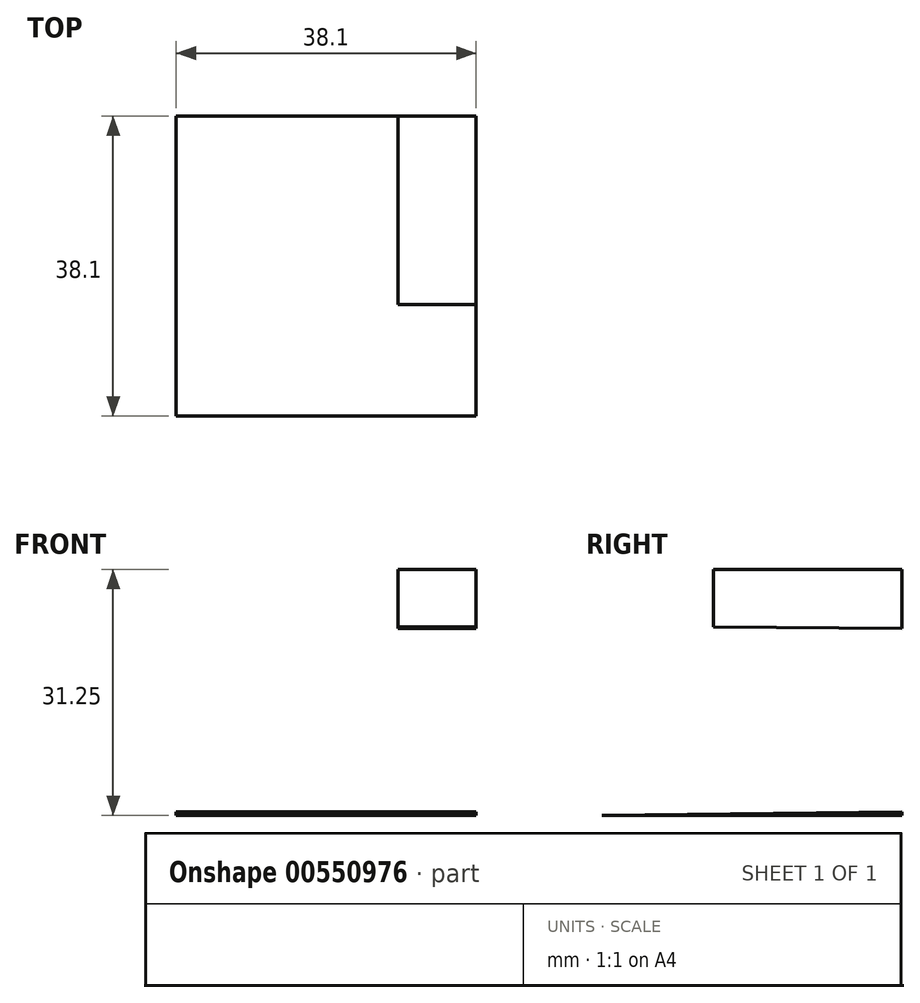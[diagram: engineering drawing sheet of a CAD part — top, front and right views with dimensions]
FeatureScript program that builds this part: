
annotation { "Feature Type Name" : "Feature", "Feature Type Description" : "" }
export const myFeature = defineFeature(function(context is Context, id is Id, definition is map)
    precondition{}
    {
        {
            var Q0;
            Q0=qCreatedBy(makeId("Front.planeOp"),FACE);
            var sketch = newSketch(context, id + "F0", { "sketchPlane" : qUnion([Q0])});
            skLineSegment(sketch, "E0", {"start": v(0, 0) * mm, "end": v(0, 38.1) * mm});
            skLineSegment(sketch, "E1", {"start": v(0, 38.1) * mm, "end": v(38.1, 38.1) * mm});
            skLineSegment(sketch, "E2", {"start": v(38.1, 38.1) * mm, "end": v(38.1, 0) * mm});
            skLineSegment(sketch, "E3", {"start": v(38.1, 0) * mm, "end": v(0, 0) * mm});
            skSolve(sketch);
        }
        {
            var Q0;
            Q0 = qSketchRegion(id + "F0", true);
            extrude(context, id + "F1", {"entities" : qUnion([Q0]), "depth" : 38.1 * mm, "offsetDistance" : 25.4 * mm});
        }
        {
            var Q0;
            Q0=qCreatedBy(makeId("Front.planeOp"),FACE);
            cPlane(context, id + "F2", {"entities" : qUnion([Q0]), "cplaneType" : CPlaneType.OFFSET, "offset" : 38.1 * mm, "width" : 152.4 * mm, "height" : 152.4 * mm});
        }
        {
            var Q0;
            Q0=makeQuery(id+"F1.opExtrude","SWEPT_FACE",FACE,{"disambiguationData":[OSD([sQuery(id+"F0.wireOp",EDGE,"E2")])]});
            var sketch = newSketch(context, id + "F3", { "sketchPlane" : qUnion([Q0])});
            skLineSegment(sketch, "E4", {"start": v(0, 38.1) * mm, "end": v(0, 15.96) * mm});
            skLineSegment(sketch, "E5", {"start": v(0, 0) * mm, "end": v(-10.74, 0) * mm});
            skLineSegment(sketch, "E6", {"start": v(-38.1, 0) * mm, "end": v(-38.1, 38.1) * mm});
            skPoint(sketch, "E7.start.orphan", {"position": v(-28.85, 0) * mm});
            skLineSegment(sketch, "E8", {"start": v(-38.1, 38.1) * mm, "end": v(-11.7, 38.1) * mm});
            skLineSegment(sketch, "E9", {"start": v(-38.1, 0) * mm, "end": v(-10.74, 0) * mm});
            skPoint(sketch, "E10.start.orphan", {"position": v(-18.83, 31.37) * mm});
            skPoint(sketch, "E11.start.orphan", {"position": v(-11.7, 22.55) * mm});
            skLineSegment(sketch, "E12", {"start": v(-38.1, 38.1) * mm, "end": v(0, 38.1) * mm});
            skLineSegment(sketch, "E13", {"start": v(0, 38.1) * mm, "end": v(0, 31.25) * mm});
            skPoint(sketch, "E14.start.orphan", {"position": v(-18.83, 18.57) * mm});
            skLineSegment(sketch, "E15", {"start": v(0, 23.74) * mm, "end": v(0, 15.96) * mm});
            skLineSegment(sketch, "E16", {"start": v(0, 0.44) * mm, "end": v(0, 0) * mm});
            skLineSegment(sketch, "E17", {"start": v(0.22, 0.44) * mm, "end": v(-38.1, 0) * mm});
            skLineSegment(sketch, "E18", {"start": v(0, 31.25) * mm, "end": v(-23.94, 31.25) * mm});
            skLineSegment(sketch, "E19", {"start": v(-23.94, 31.25) * mm, "end": v(-23.94, 23.94) * mm});
            skPoint(sketch, "E20.start.orphan", {"position": v(-18.83, 23.71) * mm});
            skLineSegment(sketch, "E21", {"start": v(-23.94, 23.94) * mm, "end": v(0, 23.74) * mm});
            skLineSegment(sketch, "E22.trimOffspring", {"start": v(0, 7.46) * mm, "end": v(0, 0) * mm});
            skPoint(sketch, "E23.end.orphan", {"position": v(-18.4, 7.46) * mm});
            skPoint(sketch, "E23.start.orphan", {"position": v(-18.83, 7.46) * mm});
            skLineSegment(sketch, "E24", {"start": v(0, 15.96) * mm, "end": v(-23.94, 16.15) * mm});
            skLineSegment(sketch, "E25", {"start": v(-23.94, 16.15) * mm, "end": v(-23.94, 7.54) * mm});
            skLineSegment(sketch, "E26", {"start": v(-23.94, 7.54) * mm, "end": v(0, 7.46) * mm});
            skLineSegment(sketch, "E27", {"start": v(0, 7.54) * mm, "end": v(0.44, -0.22) * mm});
            skLineSegment(sketch, "E28", {"start": v(0, 7.54) * mm, "end": v(0.22, 0.44) * mm});
            skSolve(sketch);
        }
        {
            var Q0;
            Q0=makeQuery(id+"F3.imprint","IMPRINT",FACE,{"disambiguationData":[TD([[makeQuery(id+"F3.imprint","IMPRINT",EDGE,{"derivedFrom":sQuery(id+"F3.wireOp",EDGE,"E4")}),-1.0]])]});
            var Q1;
            {var subQ0=sQuery(id+"F3.wireOp",EDGE,"E24");Q1=makeQuery(id+"F3.imprint","IMPRINT",FACE,{"disambiguationData":[TD([[makeQuery(id+"F3.imprint","IMPRINT",EDGE,{"derivedFrom":subQ0}),1.0]])]});}
            extrude(context, id + "F4", {"entities" : qUnion([Q0, Q1]), "operationType" : NewBodyOperationType.REMOVE, "oppositeDirection" : true, "depth" : 38.1 * mm, "offsetDistance" : 25.4 * mm});
        }
        {
            var Q0;
            Q0=qCreatedBy(id+"F2.planeOp",FACE);
            var sketch = newSketch(context, id + "F5", { "sketchPlane" : qUnion([Q0])});
            skLineSegment(sketch, "E29", {"start": v(0, 38.1) * mm, "end": v(38.1, 38.1) * mm});
            skLineSegment(sketch, "E30", {"start": v(38.1, 38.1) * mm, "end": v(38.1, 0) * mm});
            skLineSegment(sketch, "E31", {"start": v(38.1, 0) * mm, "end": v(0, 0) * mm});
            skLineSegment(sketch, "E32", {"start": v(0, 0) * mm, "end": v(0, 38.1) * mm});
            skLineSegment(sketch, "E33", {"start": v(28.2, 38.1) * mm, "end": v(28.2, 9.27) * mm});
            skLineSegment(sketch, "E34", {"start": v(28.2, 9.27) * mm, "end": v(0, 9.27) * mm});
            skLineSegment(sketch, "E35", {"start": v(0, 9.27) * mm, "end": v(0, 0) * mm});
            skLineSegment(sketch, "E36", {"start": v(0, 0) * mm, "end": v(38.1, 0) * mm});
            skLineSegment(sketch, "E37", {"start": v(38.1, 0) * mm, "end": v(38.1, 38.1) * mm});
            skLineSegment(sketch, "E38", {"start": v(38.1, 38.1) * mm, "end": v(28.2, 38.1) * mm});
            skSolve(sketch);
        }
        {
            var Q0;
            Q0=makeQuery(id+"F5.imprint","IMPRINT",FACE,{"disambiguationData":[TD([[makeQuery(id+"F5.imprint","IMPRINT",EDGE,{"derivedFrom":sQuery(id+"F5.wireOp",EDGE,"E29")}),-1.0]])]});
            extrude(context, id + "F6", {"entities" : qUnion([Q0]), "operationType" : NewBodyOperationType.REMOVE, "oppositeDirection" : true, "depth" : 38.1 * mm, "offsetDistance" : 25.4 * mm});
        }
    });
